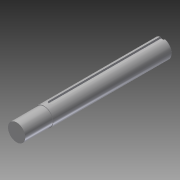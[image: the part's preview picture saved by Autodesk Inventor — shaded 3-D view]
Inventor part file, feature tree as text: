
AUTODESK INVENTOR PART (.ipt)
format: ipt  version: 2013 (Build 170138000, 138)  size: 109,056 bytes
history: native  units: in
note: dims shown in document units (in); Inventor stores cm internally (conversion verified against a paired STEP export)
features: extrude x4, sketch x3, fillet x1, chamfer x1, thread x1
ambient origin geometry x8: Origin, YZ Plane, XZ Plane, XY Plane, X Axis, Y Axis, Z Axis, Center Point
bodies: Solid1 (feature_tree)
feature tree (10):
  sketch  "Sketch1"  dims[d0=0.5in d2=0.185in]
  extrude  "Extrusion1"  Depth=0.185in
  extrude  "Extrusion2"  Depth=0.5in TaperAngle=0.0deg
  extrude  "Extrusion3"  Depth=0.75in TaperAngle=0.0deg
  extrude  "Extrusion4"  Depth=0.125in
  fillet  "Fillet1"  Radius=0.0625in
  chamfer  "Chamfer1"  Distance=3.125in
  thread  "Thread1"  [1 undecoded]
  sketch  "Sketch2"  dims[d3=3.25in d4=0.0in d5=0.5in d6=0.0in]
  sketch  "Sketch3"  dims[d7=0.4724in d9=0.75in d10=0.0in d11=0.125in d13=0.0625in d14=3.125in d15=0.0in d16=0.0625in d17=0.025in d18=0.125in d19=45.0deg d20=1.0in d21=0.0in]
note: 1 required parameter value undecoded (feature->parameter linkage not recoverable at this tier; creation-order binding heuristic only, values carry confidence <= 0.55)
